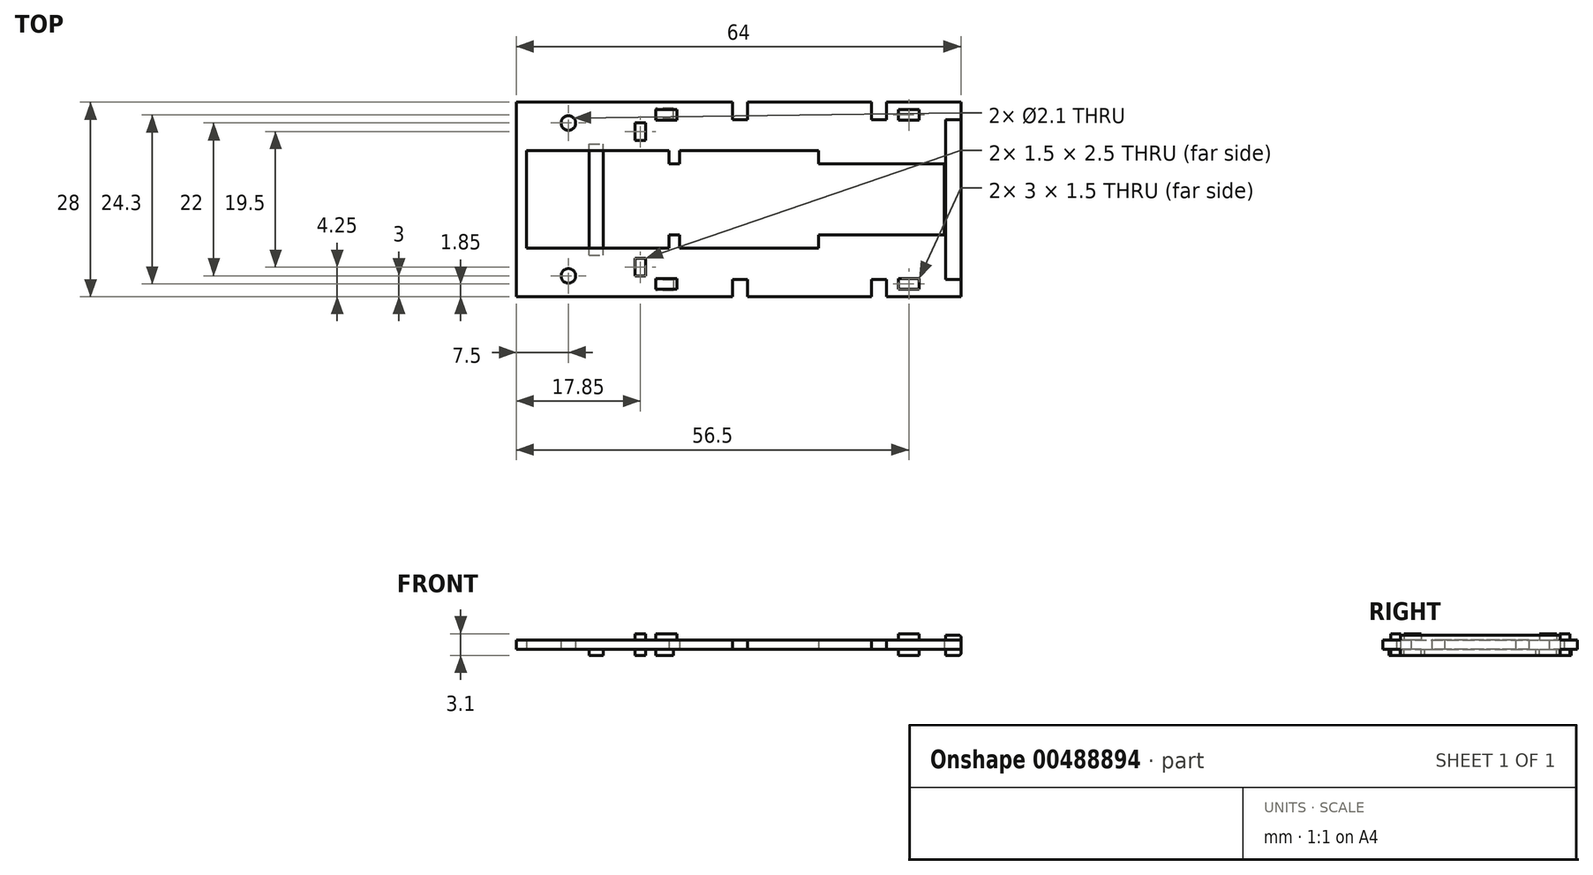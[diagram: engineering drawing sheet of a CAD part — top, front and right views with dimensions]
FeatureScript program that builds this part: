
annotation { "Feature Type Name" : "Feature", "Feature Type Description" : "" }
export const myFeature = defineFeature(function(context is Context, id is Id, definition is map)
    precondition{}
    {
        {
            var Q0;
            Q0=qCreatedBy(makeId("Top.planeOp"),FACE);
            var sketch = newSketch(context, id + "F0", { "sketchPlane" : qUnion([Q0])});
            skLineSegment(sketch, "E0.bottom", {"start": v(32, -14) * mm, "end": v(21.3, -14) * mm});
            skLineSegment(sketch, "E0.top", {"start": v(32, 14) * mm, "end": v(21.3, 14) * mm});
            skLineSegment(sketch, "E0.left", {"start": v(32, -14) * mm, "end": v(32, 14) * mm});
            skLineSegment(sketch, "E0.right", {"start": v(-32, -14) * mm, "end": v(-32, 14) * mm});
            skPoint(sketch, "E0.middle", {"position": v(0, 0) * mm});
            skLineSegment(sketch, "E1.bottom", {"start": v(-10, 5.1) * mm, "end": v(-8.5, 5.1) * mm});
            skLineSegment(sketch, "E1.top", {"start": v(-10, -5.1) * mm, "end": v(-8.5, -5.1) * mm});
            skLineSegment(sketch, "E1.left", {"start": v(-30.5, 5.1) * mm, "end": v(-30.5, -5.1) * mm});
            skLineSegment(sketch, "E1.right", {"start": v(29.6, 5.1) * mm, "end": v(29.6, -5.1) * mm});
            skLineSegment(sketch, "E2.bottom", {"start": v(-30.5, 7) * mm, "end": v(-10, 7) * mm});
            skLineSegment(sketch, "E2.top", {"start": v(-30.5, -7) * mm, "end": v(-10, -7) * mm});
            skLineSegment(sketch, "E2.left", {"start": v(-30.5, 7) * mm, "end": v(-30.5, 5.1) * mm});
            skLineSegment(sketch, "E2.right", {"start": v(11.5, 7) * mm, "end": v(11.5, 5.1) * mm});
            skLineSegment(sketch, "E3.left", {"start": v(-10, 7) * mm, "end": v(-10, 5.1) * mm});
            skLineSegment(sketch, "E3.right", {"start": v(-8.5, 7) * mm, "end": v(-8.5, 5.1) * mm});
            skLineSegment(sketch, "E4.trimOffspring", {"start": v(-10, -5.1) * mm, "end": v(-10, -7) * mm});
            skLineSegment(sketch, "E5.trimOffspring", {"start": v(11.5, 5.1) * mm, "end": v(29.6, 5.1) * mm});
            skLineSegment(sketch, "E6.trimOffspring", {"start": v(11.5, -5.1) * mm, "end": v(29.6, -5.1) * mm});
            skLineSegment(sketch, "E7.trimOffspring", {"start": v(-8.5, -7) * mm, "end": v(11.5, -7) * mm});
            skLineSegment(sketch, "E8.trimOffspring", {"start": v(-8.5, 7) * mm, "end": v(11.5, 7) * mm});
            skLineSegment(sketch, "E9.trimOffspring", {"start": v(-8.5, -5.1) * mm, "end": v(-8.5, -7) * mm});
            skLineSegment(sketch, "E10.trimOffspring", {"start": v(11.5, -5.1) * mm, "end": v(11.5, -7) * mm});
            skLineSegment(sketch, "E11.trimOffspring", {"start": v(-30.5, -5.1) * mm, "end": v(-30.5, -7) * mm});
            skCircle(sketch, "E12", {"center": v(-24.5, -11) * mm, "radius": 1.05 * mm});
            skCircle(sketch, "E13.MirrorC", {"center": v(-24.5, 11) * mm, "radius": 1.05 * mm});
            skLineSegment(sketch, "E14.bottom", {"start": v(-0.9, -11.5) * mm, "end": v(1.3, -11.5) * mm});
            skLineSegment(sketch, "E14.left", {"start": v(-0.9, -11.5) * mm, "end": v(-0.9, -14) * mm});
            skLineSegment(sketch, "E14.right", {"start": v(1.3, -11.5) * mm, "end": v(1.3, -14) * mm});
            skLineSegment(sketch, "E15.top", {"start": v(19.1, -11.5) * mm, "end": v(21.3, -11.5) * mm});
            skLineSegment(sketch, "E15.left", {"start": v(19.1, -14) * mm, "end": v(19.1, -11.5) * mm});
            skLineSegment(sketch, "E15.right", {"start": v(21.3, -14) * mm, "end": v(21.3, -11.5) * mm});
            skLineSegment(sketch, "E16.MirrorCS", {"start": v(21.3, 14) * mm, "end": v(21.3, 11.5) * mm});
            skLineSegment(sketch, "E17.MirrorCS", {"start": v(-0.9, 11.5) * mm, "end": v(-0.9, 14) * mm});
            skLineSegment(sketch, "E18.MirrorCS", {"start": v(19.1, 14) * mm, "end": v(19.1, 11.5) * mm});
            skLineSegment(sketch, "E19.MirrorCS", {"start": v(1.3, 11.5) * mm, "end": v(1.3, 14) * mm});
            skLineSegment(sketch, "E20.MirrorCS", {"start": v(19.1, 11.5) * mm, "end": v(21.3, 11.5) * mm});
            skLineSegment(sketch, "E21.MirrorCS", {"start": v(-0.9, 11.5) * mm, "end": v(1.3, 11.5) * mm});
            skLineSegment(sketch, "E22.trimOffspring", {"start": v(-0.9, 14) * mm, "end": v(-32, 14) * mm});
            skLineSegment(sketch, "E23.trimOffspring", {"start": v(19.1, 14) * mm, "end": v(1.3, 14) * mm});
            skLineSegment(sketch, "E24.trimOffspring", {"start": v(19.1, -14) * mm, "end": v(1.3, -14) * mm});
            skLineSegment(sketch, "E25.trimOffspring", {"start": v(-0.9, -14) * mm, "end": v(-32, -14) * mm});
            skPoint(sketch, "E26.middle", {"position": v(12.9, 2.69) * mm});
            skSolve(sketch);
        }
        {
            var Q0;
            Q0=makeQuery(id+"F0.imprint","IMPRINT",FACE,{"disambiguationData":[TD([[makeQuery(id+"F0.imprint","IMPRINT",EDGE,{"derivedFrom":sQuery(id+"F0.wireOp",EDGE,"E0.bottom")}),-1.0]])]});
            extrude(context, id + "F1", {"entities" : qUnion([Q0]), "depth" : 1.3 * mm});
        }
        {
            var Q0;
            Q0=makeQuery(id+"F1.opExtrude","CAP_FACE",FACE,{"disambiguationData":[OSD([sQuery(id+"F0.wireOp",EDGE,"E0.bottom"),sQuery(id+"F0.wireOp",EDGE,"E0.top"),sQuery(id+"F0.wireOp",EDGE,"E0.left"),sQuery(id+"F0.wireOp",EDGE,"E0.right"),sQuery(id+"F0.wireOp",EDGE,"E1.bottom"),sQuery(id+"F0.wireOp",EDGE,"E1.top"),sQuery(id+"F0.wireOp",EDGE,"E1.left"),sQuery(id+"F0.wireOp",EDGE,"E1.right"),sQuery(id+"F0.wireOp",EDGE,"E2.bottom"),sQuery(id+"F0.wireOp",EDGE,"E2.top"),sQuery(id+"F0.wireOp",EDGE,"E2.left"),sQuery(id+"F0.wireOp",EDGE,"E2.right"),sQuery(id+"F0.wireOp",EDGE,"E3.left"),sQuery(id+"F0.wireOp",EDGE,"E3.right"),sQuery(id+"F0.wireOp",EDGE,"E4.trimOffspring"),sQuery(id+"F0.wireOp",EDGE,"E5.trimOffspring"),sQuery(id+"F0.wireOp",EDGE,"E6.trimOffspring"),sQuery(id+"F0.wireOp",EDGE,"E7.trimOffspring"),sQuery(id+"F0.wireOp",EDGE,"E8.trimOffspring"),sQuery(id+"F0.wireOp",EDGE,"E9.trimOffspring"),sQuery(id+"F0.wireOp",EDGE,"E10.trimOffspring"),sQuery(id+"F0.wireOp",EDGE,"E11.trimOffspring"),sQuery(id+"F0.wireOp",EDGE,"E12"),sQuery(id+"F0.wireOp",EDGE,"E13.MirrorC"),sQuery(id+"F0.wireOp",EDGE,"E14.bottom"),sQuery(id+"F0.wireOp",EDGE,"E14.left"),sQuery(id+"F0.wireOp",EDGE,"E14.right"),sQuery(id+"F0.wireOp",EDGE,"E15.top"),sQuery(id+"F0.wireOp",EDGE,"E15.left"),sQuery(id+"F0.wireOp",EDGE,"E15.right"),sQuery(id+"F0.wireOp",EDGE,"E16.MirrorCS"),sQuery(id+"F0.wireOp",EDGE,"E17.MirrorCS"),sQuery(id+"F0.wireOp",EDGE,"E18.MirrorCS"),sQuery(id+"F0.wireOp",EDGE,"E19.MirrorCS"),sQuery(id+"F0.wireOp",EDGE,"E20.MirrorCS"),sQuery(id+"F0.wireOp",EDGE,"E21.MirrorCS"),sQuery(id+"F0.wireOp",EDGE,"E22.trimOffspring"),sQuery(id+"F0.wireOp",EDGE,"E23.trimOffspring"),sQuery(id+"F0.wireOp",EDGE,"E24.trimOffspring"),sQuery(id+"F0.wireOp",EDGE,"E25.trimOffspring")])],"isStart":false});
            var sketch = newSketch(context, id + "F2", { "sketchPlane" : qUnion([Q0])});
            skLineSegment(sketch, "E27.bottom", {"start": v(-5.8, -1.39) * mm, "end": v(-6.3, -1.39) * mm});
            skLineSegment(sketch, "E27.top", {"start": v(-5.8, 1.39) * mm, "end": v(-6.3, 1.39) * mm});
            skLineSegment(sketch, "E27.left", {"start": v(-5.8, -1.39) * mm, "end": v(-5.8, 1.39) * mm});
            skLineSegment(sketch, "E27.right", {"start": v(-6.3, -1.39) * mm, "end": v(-6.3, 1.39) * mm});
            skPoint(sketch, "E27.middle", {"position": v(-6.05, 0) * mm});
            skLineSegment(sketch, "E28.bottom", {"start": v(29.7, -11.3) * mm, "end": v(-13.3, -11.3) * mm});
            skLineSegment(sketch, "E28.top", {"start": v(29.7, 11.3) * mm, "end": v(-13.3, 11.3) * mm});
            skLineSegment(sketch, "E28.left", {"start": v(29.7, -11.3) * mm, "end": v(29.7, 11.3) * mm});
            skLineSegment(sketch, "E28.right", {"start": v(-13.3, -11.3) * mm, "end": v(-13.3, 11.3) * mm});
            skPoint(sketch, "E28.middle", {"position": v(8.2, 0) * mm});
            skLineSegment(sketch, "E29.bottom", {"start": v(-5.6, -0.5) * mm, "end": v(-6.5, -0.5) * mm});
            skLineSegment(sketch, "E29.top", {"start": v(-5.6, 0.5) * mm, "end": v(-6.5, 0.5) * mm});
            skLineSegment(sketch, "E29.left", {"start": v(-5.6, -0.5) * mm, "end": v(-5.6, 0.5) * mm});
            skLineSegment(sketch, "E29.right", {"start": v(-6.5, -0.5) * mm, "end": v(-6.5, 0.5) * mm});
            skSolve(sketch);
        }
        {
            var Q0;
            {var subQ1=sQuery(id+"F2.wireOp",EDGE,"E28.bottom");Q0=makeQuery(id+"F2.imprint","IMPRINT",FACE,{"disambiguationData":[TD([[makeQuery(id+"F2.imprint","IMPRINT",EDGE,{"derivedFrom":subQ1}),1.0]])]});}
            var sketch = newSketch(context, id + "F3", { "sketchPlane" : qUnion([Q0])});
            skLineSegment(sketch, "E30.bottom", {"start": v(32, -11.5) * mm, "end": v(29.8, -11.5) * mm});
            skLineSegment(sketch, "E30.top", {"start": v(32, 11.5) * mm, "end": v(29.8, 11.5) * mm});
            skLineSegment(sketch, "E30.left", {"start": v(32, -11.5) * mm, "end": v(32, 11.5) * mm});
            skLineSegment(sketch, "E30.right", {"start": v(29.8, -11.5) * mm, "end": v(29.8, 11.5) * mm});
            skPoint(sketch, "E30.middle", {"position": v(30.9, 0) * mm});
            skLineSegment(sketch, "E31.bottom", {"start": v(23, 12.9) * mm, "end": v(26, 12.9) * mm});
            skLineSegment(sketch, "E31.top", {"start": v(23, 11.4) * mm, "end": v(26, 11.4) * mm});
            skLineSegment(sketch, "E31.left", {"start": v(23, 12.9) * mm, "end": v(23, 11.4) * mm});
            skLineSegment(sketch, "E31.right", {"start": v(26, 12.9) * mm, "end": v(26, 11.4) * mm});
            skLineSegment(sketch, "E32.MirrorCS", {"start": v(23, -11.4) * mm, "end": v(26, -11.4) * mm});
            skLineSegment(sketch, "E33.MirrorCS", {"start": v(23, -12.9) * mm, "end": v(23, -11.4) * mm});
            skLineSegment(sketch, "E34.MirrorCS", {"start": v(23, -12.9) * mm, "end": v(26, -12.9) * mm});
            skLineSegment(sketch, "E35.MirrorCS", {"start": v(26, -12.9) * mm, "end": v(26, -11.4) * mm});
            skLineSegment(sketch, "E36.bottom", {"start": v(-14.9, -8.5) * mm, "end": v(-13.4, -8.5) * mm});
            skLineSegment(sketch, "E36.top", {"start": v(-14.9, -11) * mm, "end": v(-13.4, -11) * mm});
            skLineSegment(sketch, "E36.left", {"start": v(-14.9, -8.5) * mm, "end": v(-14.9, -11) * mm});
            skLineSegment(sketch, "E36.right", {"start": v(-13.4, -8.5) * mm, "end": v(-13.4, -11) * mm});
            skLineSegment(sketch, "E37.bottom", {"start": v(-11.9, -11.4) * mm, "end": v(-8.9, -11.4) * mm});
            skLineSegment(sketch, "E37.top", {"start": v(-11.9, -12.9) * mm, "end": v(-8.9, -12.9) * mm});
            skLineSegment(sketch, "E37.left", {"start": v(-11.9, -11.4) * mm, "end": v(-11.9, -12.9) * mm});
            skLineSegment(sketch, "E37.right", {"start": v(-8.9, -11.4) * mm, "end": v(-8.9, -12.9) * mm});
            skLineSegment(sketch, "E38.MirrorCS", {"start": v(-11.9, 11.4) * mm, "end": v(-11.9, 12.9) * mm});
            skLineSegment(sketch, "E39.MirrorCS", {"start": v(-8.9, 11.4) * mm, "end": v(-8.9, 12.9) * mm});
            skLineSegment(sketch, "E40.MirrorCS", {"start": v(-11.9, 11.4) * mm, "end": v(-8.9, 11.4) * mm});
            skLineSegment(sketch, "E41.MirrorCS", {"start": v(-11.9, 12.9) * mm, "end": v(-8.9, 12.9) * mm});
            skLineSegment(sketch, "E42.MirrorCS", {"start": v(-14.9, 11) * mm, "end": v(-13.4, 11) * mm});
            skLineSegment(sketch, "E43.MirrorCS", {"start": v(-14.9, 8.5) * mm, "end": v(-14.9, 11) * mm});
            skLineSegment(sketch, "E44.MirrorCS", {"start": v(-14.9, 8.5) * mm, "end": v(-13.4, 8.5) * mm});
            skLineSegment(sketch, "E45.MirrorCS", {"start": v(-13.4, 8.5) * mm, "end": v(-13.4, 11) * mm});
            skSolve(sketch);
        }
        {
            var Q0;
            Q0=makeQuery(id+"F3.imprint","IMPRINT",FACE,{"disambiguationData":[TD([[makeQuery(id+"F3.imprint","IMPRINT",EDGE,{"derivedFrom":sQuery(id+"F3.wireOp",EDGE,"E30.bottom")}),-1.0]])]});
            extrude(context, id + "F4", {"entities" : qUnion([Q0]), "operationType" : NewBodyOperationType.ADD, "depth" : 0.7 * mm, "offsetDistance" : 25 * mm});
        }
        {
            var Q0;
            Q0=makeQuery(id+"F1.opExtrude","CAP_FACE",FACE,{"disambiguationData":[OSD([sQuery(id+"F0.wireOp",EDGE,"E0.bottom"),sQuery(id+"F0.wireOp",EDGE,"E0.top"),sQuery(id+"F0.wireOp",EDGE,"E0.left"),sQuery(id+"F0.wireOp",EDGE,"E0.right"),sQuery(id+"F0.wireOp",EDGE,"E1.bottom"),sQuery(id+"F0.wireOp",EDGE,"E1.top"),sQuery(id+"F0.wireOp",EDGE,"E1.left"),sQuery(id+"F0.wireOp",EDGE,"E1.right"),sQuery(id+"F0.wireOp",EDGE,"E2.bottom"),sQuery(id+"F0.wireOp",EDGE,"E2.top"),sQuery(id+"F0.wireOp",EDGE,"E2.left"),sQuery(id+"F0.wireOp",EDGE,"E2.right"),sQuery(id+"F0.wireOp",EDGE,"E3.left"),sQuery(id+"F0.wireOp",EDGE,"E3.right"),sQuery(id+"F0.wireOp",EDGE,"E4.trimOffspring"),sQuery(id+"F0.wireOp",EDGE,"E5.trimOffspring"),sQuery(id+"F0.wireOp",EDGE,"E6.trimOffspring"),sQuery(id+"F0.wireOp",EDGE,"E7.trimOffspring"),sQuery(id+"F0.wireOp",EDGE,"E8.trimOffspring"),sQuery(id+"F0.wireOp",EDGE,"E9.trimOffspring"),sQuery(id+"F0.wireOp",EDGE,"E10.trimOffspring"),sQuery(id+"F0.wireOp",EDGE,"E11.trimOffspring"),sQuery(id+"F0.wireOp",EDGE,"E12"),sQuery(id+"F0.wireOp",EDGE,"E13.MirrorC"),sQuery(id+"F0.wireOp",EDGE,"E14.bottom"),sQuery(id+"F0.wireOp",EDGE,"E14.left"),sQuery(id+"F0.wireOp",EDGE,"E14.right"),sQuery(id+"F0.wireOp",EDGE,"E15.top"),sQuery(id+"F0.wireOp",EDGE,"E15.left"),sQuery(id+"F0.wireOp",EDGE,"E15.right"),sQuery(id+"F0.wireOp",EDGE,"E16.MirrorCS"),sQuery(id+"F0.wireOp",EDGE,"E17.MirrorCS"),sQuery(id+"F0.wireOp",EDGE,"E18.MirrorCS"),sQuery(id+"F0.wireOp",EDGE,"E19.MirrorCS"),sQuery(id+"F0.wireOp",EDGE,"E20.MirrorCS"),sQuery(id+"F0.wireOp",EDGE,"E21.MirrorCS"),sQuery(id+"F0.wireOp",EDGE,"E22.trimOffspring"),sQuery(id+"F0.wireOp",EDGE,"E23.trimOffspring"),sQuery(id+"F0.wireOp",EDGE,"E24.trimOffspring"),sQuery(id+"F0.wireOp",EDGE,"E25.trimOffspring")])],"isStart":true});
            var sketch = newSketch(context, id + "F5", { "sketchPlane" : qUnion([Q0])});
            skLineSegment(sketch, "E46.bottom", {"start": v(32, 11.5) * mm, "end": v(29.8, 11.5) * mm});
            skLineSegment(sketch, "E46.top", {"start": v(32, -11.5) * mm, "end": v(29.8, -11.5) * mm});
            skLineSegment(sketch, "E46.left", {"start": v(32, 11.5) * mm, "end": v(32, -11.5) * mm});
            skLineSegment(sketch, "E46.right", {"start": v(29.8, 11.5) * mm, "end": v(29.8, -11.5) * mm});
            skPoint(sketch, "E46.middle", {"position": v(30.9, 0) * mm});
            skPoint(sketch, "E46.middle.positionSnap0", {"position": v(32, 0) * mm});
            skPoint(sketch, "E46.centerSnap0", {"position": v(32, 0) * mm});
            skLineSegment(sketch, "E47.bottom", {"start": v(26, 11.4) * mm, "end": v(23, 11.4) * mm});
            skLineSegment(sketch, "E47.top", {"start": v(26, 12.9) * mm, "end": v(23, 12.9) * mm});
            skLineSegment(sketch, "E47.left", {"start": v(26, 11.4) * mm, "end": v(26, 12.9) * mm});
            skLineSegment(sketch, "E47.right", {"start": v(23, 11.4) * mm, "end": v(23, 12.9) * mm});
            skLineSegment(sketch, "E48.bottom", {"start": v(-13.4, 8.5) * mm, "end": v(-14.9, 8.5) * mm});
            skLineSegment(sketch, "E48.top", {"start": v(-13.4, 11) * mm, "end": v(-14.9, 11) * mm});
            skLineSegment(sketch, "E48.left", {"start": v(-13.4, 8.5) * mm, "end": v(-13.4, 11) * mm});
            skLineSegment(sketch, "E48.right", {"start": v(-14.9, 8.5) * mm, "end": v(-14.9, 11) * mm});
            skLineSegment(sketch, "E49.bottom", {"start": v(-9.4, 11.6) * mm, "end": v(-11.9, 11.6) * mm});
            skLineSegment(sketch, "E49.top", {"start": v(-9.4, 13.1) * mm, "end": v(-11.9, 13.1) * mm});
            skLineSegment(sketch, "E49.left", {"start": v(-9.4, 11.6) * mm, "end": v(-9.4, 13.1) * mm});
            skLineSegment(sketch, "E49.right", {"start": v(-11.9, 11.6) * mm, "end": v(-11.9, 13.1) * mm});
            skLineSegment(sketch, "E50.MirrorCS", {"start": v(-13.4, -11) * mm, "end": v(-14.9, -11) * mm});
            skLineSegment(sketch, "E51.MirrorCS", {"start": v(23, -11.4) * mm, "end": v(23, -12.9) * mm});
            skLineSegment(sketch, "E52.MirrorCS", {"start": v(-11.9, -11.6) * mm, "end": v(-11.9, -13.1) * mm});
            skLineSegment(sketch, "E53.MirrorCS", {"start": v(-9.4, -11.6) * mm, "end": v(-9.4, -13.1) * mm});
            skLineSegment(sketch, "E54.MirrorCS", {"start": v(-13.4, -8.5) * mm, "end": v(-14.9, -8.5) * mm});
            skLineSegment(sketch, "E55.MirrorCS", {"start": v(26, -11.4) * mm, "end": v(26, -12.9) * mm});
            skLineSegment(sketch, "E56.MirrorCS", {"start": v(-13.4, -8.5) * mm, "end": v(-13.4, -11) * mm});
            skLineSegment(sketch, "E57.MirrorCS", {"start": v(-9.4, -13.1) * mm, "end": v(-11.9, -13.1) * mm});
            skLineSegment(sketch, "E58.MirrorCS", {"start": v(26, -11.4) * mm, "end": v(23, -11.4) * mm});
            skLineSegment(sketch, "E59.MirrorCS", {"start": v(-14.9, -8.5) * mm, "end": v(-14.9, -11) * mm});
            skLineSegment(sketch, "E60.MirrorCS", {"start": v(26, -12.9) * mm, "end": v(23, -12.9) * mm});
            skLineSegment(sketch, "E61.MirrorCS", {"start": v(-9.4, -11.6) * mm, "end": v(-11.9, -11.6) * mm});
            skSolve(sketch);
        }
        {
            var Q0;
            Q0=makeQuery(id+"F5.imprint","IMPRINT",FACE,{"disambiguationData":[TD([[makeQuery(id+"F5.imprint","IMPRINT",EDGE,{"derivedFrom":sQuery(id+"F5.wireOp",EDGE,"E49.bottom")}),-1.0]])]});
            var Q1;
            Q1=makeQuery(id+"F5.imprint","IMPRINT",FACE,{"disambiguationData":[TD([[makeQuery(id+"F5.imprint","IMPRINT",EDGE,{"derivedFrom":sQuery(id+"F5.wireOp",EDGE,"E48.bottom")}),-1.0]])]});
            var Q2;
            Q2=makeQuery(id+"F5.imprint","IMPRINT",FACE,{"disambiguationData":[TD([[makeQuery(id+"F5.imprint","IMPRINT",EDGE,{"derivedFrom":sQuery(id+"F5.wireOp",EDGE,"E50.MirrorCS")}),-1.0]])]});
            var Q3;
            Q3=makeQuery(id+"F5.imprint","IMPRINT",FACE,{"disambiguationData":[TD([[makeQuery(id+"F5.imprint","IMPRINT",EDGE,{"derivedFrom":sQuery(id+"F5.wireOp",EDGE,"E52.MirrorCS")}),1.0]])]});
            var Q4;
            Q4=makeQuery(id+"F5.imprint","IMPRINT",FACE,{"disambiguationData":[TD([[makeQuery(id+"F5.imprint","IMPRINT",EDGE,{"derivedFrom":sQuery(id+"F5.wireOp",EDGE,"E51.MirrorCS")}),1.0]])]});
            var Q5;
            Q5=makeQuery(id+"F5.imprint","IMPRINT",FACE,{"disambiguationData":[TD([[makeQuery(id+"F5.imprint","IMPRINT",EDGE,{"derivedFrom":sQuery(id+"F5.wireOp",EDGE,"E46.bottom")}),1.0]])]});
            var Q6;
            Q6=makeQuery(id+"F5.imprint","IMPRINT",FACE,{"disambiguationData":[TD([[makeQuery(id+"F5.imprint","IMPRINT",EDGE,{"derivedFrom":sQuery(id+"F5.wireOp",EDGE,"E47.bottom")}),-1.0]])]});
            extrude(context, id + "F6", {"entities" : qUnion([Q0, Q1, Q2, Q3, Q4, Q5, Q6]), "operationType" : NewBodyOperationType.ADD, "depth" : 0.9 * mm, "offsetDistance" : 25 * mm});
        }
        {
            var Q0;
            Q0=makeQuery(id+"F6.opExtrude","CAP_EDGE",EDGE,{"disambiguationData":[OSD([sQuery(id+"F5.wireOp",EDGE,"E46.left")])],"isStart":false});
            fillet(context, id + "F7", {"entities" : qUnion([Q0]), "radius" : 0.3 * mm, "tangentPropagation" : true, "allowEdgeOverflow" : false});
        }
        {
            var Q0;
            Q0=makeQuery(id+"F4.opExtrude","CAP_EDGE",EDGE,{"disambiguationData":[OSD([sQuery(id+"F3.wireOp",EDGE,"E30.left")])],"isStart":false});
            fillet(context, id + "F8", {"entities" : qUnion([Q0]), "radius" : 0.3 * mm, "tangentPropagation" : true, "allowEdgeOverflow" : false});
        }
        {
            var Q0;
            Q0=makeQuery(id+"F1.opExtrude","CAP_FACE",FACE,{"disambiguationData":[OSD([sQuery(id+"F0.wireOp",EDGE,"E0.bottom"),sQuery(id+"F0.wireOp",EDGE,"E0.top"),sQuery(id+"F0.wireOp",EDGE,"E0.left"),sQuery(id+"F0.wireOp",EDGE,"E0.right"),sQuery(id+"F0.wireOp",EDGE,"E1.bottom"),sQuery(id+"F0.wireOp",EDGE,"E1.top"),sQuery(id+"F0.wireOp",EDGE,"E1.left"),sQuery(id+"F0.wireOp",EDGE,"E1.right"),sQuery(id+"F0.wireOp",EDGE,"E2.bottom"),sQuery(id+"F0.wireOp",EDGE,"E2.top"),sQuery(id+"F0.wireOp",EDGE,"E2.left"),sQuery(id+"F0.wireOp",EDGE,"E2.right"),sQuery(id+"F0.wireOp",EDGE,"E3.left"),sQuery(id+"F0.wireOp",EDGE,"E3.right"),sQuery(id+"F0.wireOp",EDGE,"E4.trimOffspring"),sQuery(id+"F0.wireOp",EDGE,"E5.trimOffspring"),sQuery(id+"F0.wireOp",EDGE,"E6.trimOffspring"),sQuery(id+"F0.wireOp",EDGE,"E7.trimOffspring"),sQuery(id+"F0.wireOp",EDGE,"E8.trimOffspring"),sQuery(id+"F0.wireOp",EDGE,"E9.trimOffspring"),sQuery(id+"F0.wireOp",EDGE,"E10.trimOffspring"),sQuery(id+"F0.wireOp",EDGE,"E11.trimOffspring"),sQuery(id+"F0.wireOp",EDGE,"E12"),sQuery(id+"F0.wireOp",EDGE,"E13.MirrorC"),sQuery(id+"F0.wireOp",EDGE,"E14.bottom"),sQuery(id+"F0.wireOp",EDGE,"E14.left"),sQuery(id+"F0.wireOp",EDGE,"E14.right"),sQuery(id+"F0.wireOp",EDGE,"E15.top"),sQuery(id+"F0.wireOp",EDGE,"E15.left"),sQuery(id+"F0.wireOp",EDGE,"E15.right"),sQuery(id+"F0.wireOp",EDGE,"E16.MirrorCS"),sQuery(id+"F0.wireOp",EDGE,"E17.MirrorCS"),sQuery(id+"F0.wireOp",EDGE,"E18.MirrorCS"),sQuery(id+"F0.wireOp",EDGE,"E19.MirrorCS"),sQuery(id+"F0.wireOp",EDGE,"E20.MirrorCS"),sQuery(id+"F0.wireOp",EDGE,"E21.MirrorCS"),sQuery(id+"F0.wireOp",EDGE,"E22.trimOffspring"),sQuery(id+"F0.wireOp",EDGE,"E23.trimOffspring"),sQuery(id+"F0.wireOp",EDGE,"E24.trimOffspring"),sQuery(id+"F0.wireOp",EDGE,"E25.trimOffspring")])],"isStart":true});
            var sketch = newSketch(context, id + "F9", { "sketchPlane" : qUnion([Q0])});
            skLineSegment(sketch, "E62.bottom", {"start": v(-21.5, 8) * mm, "end": v(-19.5, 8) * mm});
            skLineSegment(sketch, "E62.top", {"start": v(-21.5, -8) * mm, "end": v(-19.5, -8) * mm});
            skLineSegment(sketch, "E62.left", {"start": v(-21.5, 8) * mm, "end": v(-21.5, -8) * mm});
            skLineSegment(sketch, "E62.right", {"start": v(-19.5, 8) * mm, "end": v(-19.5, -8) * mm});
            skSolve(sketch);
        }
        {
            var Q0;
            {var subQ0=sQuery(id+"F9.wireOp",EDGE,"E62.bottom");Q0=makeQuery(id+"F9.imprint","IMPRINT",FACE,{"disambiguationData":[TD([[makeQuery(id+"F9.imprint","IMPRINT",EDGE,{"derivedFrom":subQ0}),-1.0]])]});}
            var Q1;
            {var subQ0=sQuery(id+"F9.wireOp",EDGE,"E62.top");Q1=makeQuery(id+"F9.imprint","IMPRINT",FACE,{"disambiguationData":[TD([[makeQuery(id+"F9.imprint","IMPRINT",EDGE,{"derivedFrom":subQ0}),1.0]])]});}
            var Q2;
            {var subQ0=sQuery(id+"F9.wireOp",EDGE,"E62.left");var subQ1=makeQuery(id+"F1.opExtrude","CAP_EDGE",EDGE,{"disambiguationData":[OSD([sQuery(id+"F0.wireOp",EDGE,"E2.top")])],"isStart":true});var subQ2=makeQuery(id+"F9.imprint","INTERSECT",VERTEX,{"derivedFrom":[subQ1,subQ0]});Q2=makeQuery(id+"F9.imprint","IMPRINT",FACE,{"disambiguationData":[TD([[makeQuery(id+"F9.imprint","IMPRINT",EDGE,{"disambiguationData":[TD([[subQ2,-1.0]])],"derivedFrom":subQ0}),1.0]])]});}
            extrude(context, id + "F10", {"entities" : qUnion([Q0, Q1, Q2]), "operationType" : NewBodyOperationType.ADD, "depth" : 0.9 * mm, "offsetDistance" : 25 * mm});
        }
        {
            var Q0;
            Q0=makeQuery(id+"F3.imprint","IMPRINT",FACE,{"disambiguationData":[TD([[makeQuery(id+"F3.imprint","IMPRINT",EDGE,{"derivedFrom":sQuery(id+"F3.wireOp",EDGE,"E38.MirrorCS")}),-1.0]])]});
            var Q1;
            Q1=makeQuery(id+"F3.imprint","IMPRINT",FACE,{"disambiguationData":[TD([[makeQuery(id+"F3.imprint","IMPRINT",EDGE,{"derivedFrom":sQuery(id+"F3.wireOp",EDGE,"E42.MirrorCS")}),-1.0]])]});
            var Q2;
            Q2=makeQuery(id+"F3.imprint","IMPRINT",FACE,{"disambiguationData":[TD([[makeQuery(id+"F3.imprint","IMPRINT",EDGE,{"derivedFrom":sQuery(id+"F3.wireOp",EDGE,"E36.bottom")}),-1.0]])]});
            var Q3;
            Q3=makeQuery(id+"F3.imprint","IMPRINT",FACE,{"disambiguationData":[TD([[makeQuery(id+"F3.imprint","IMPRINT",EDGE,{"derivedFrom":sQuery(id+"F3.wireOp",EDGE,"E37.bottom")}),-1.0]])]});
            var Q4;
            Q4=makeQuery(id+"F3.imprint","IMPRINT",FACE,{"disambiguationData":[TD([[makeQuery(id+"F3.imprint","IMPRINT",EDGE,{"derivedFrom":sQuery(id+"F3.wireOp",EDGE,"E32.MirrorCS")}),-1.0]])]});
            var Q5;
            Q5=makeQuery(id+"F3.imprint","IMPRINT",FACE,{"disambiguationData":[TD([[makeQuery(id+"F3.imprint","IMPRINT",EDGE,{"derivedFrom":sQuery(id+"F3.wireOp",EDGE,"E31.bottom")}),-1.0]])]});
            extrude(context, id + "F11", {"entities" : qUnion([Q0, Q1, Q2, Q3, Q4, Q5]), "operationType" : NewBodyOperationType.ADD, "depth" : 0.9 * mm, "offsetDistance" : 25 * mm});
        }
    });
